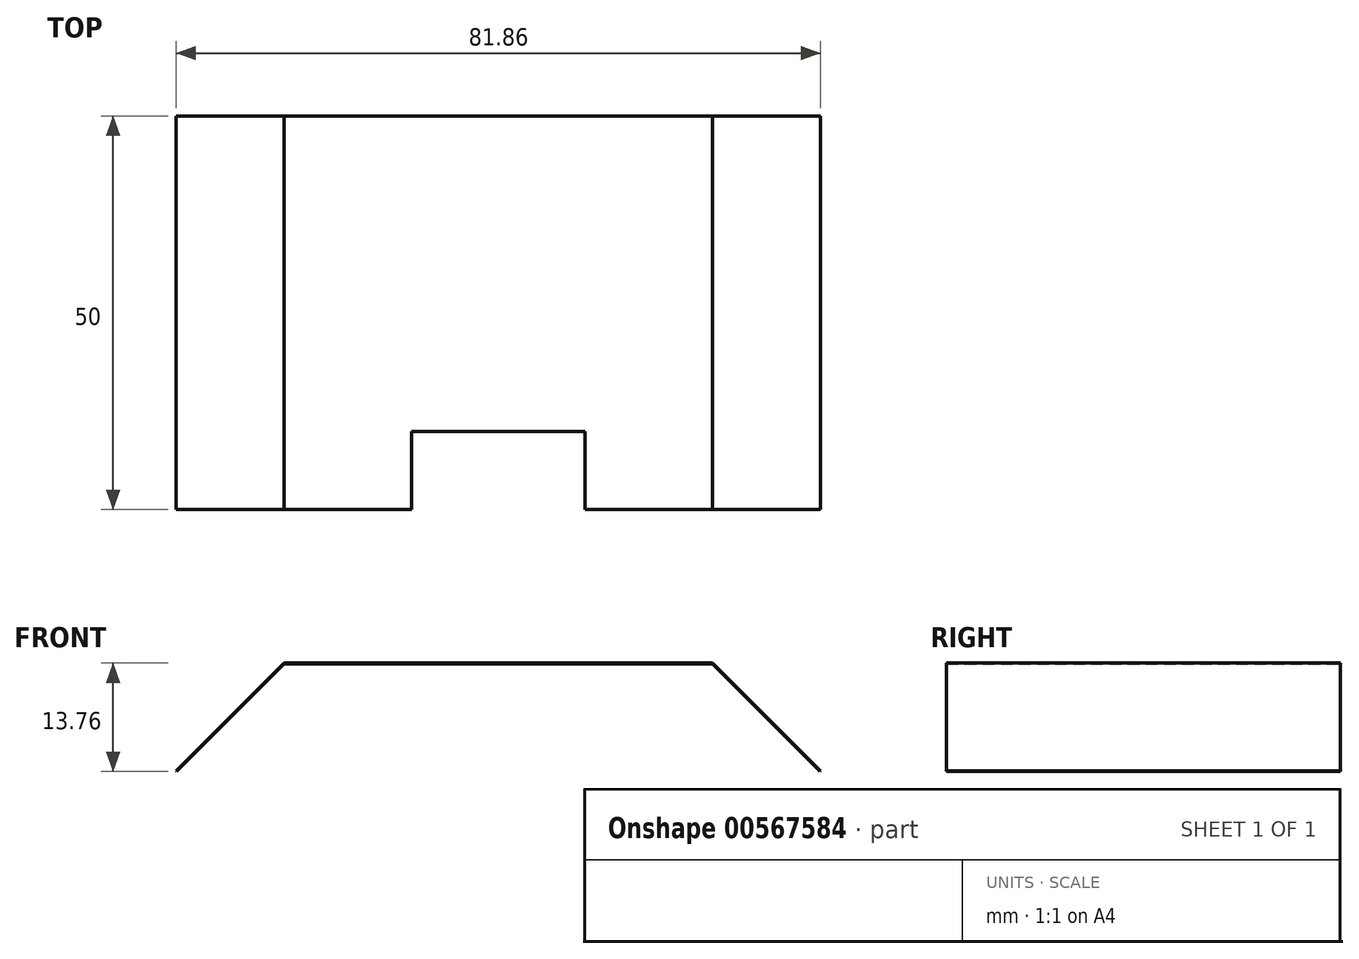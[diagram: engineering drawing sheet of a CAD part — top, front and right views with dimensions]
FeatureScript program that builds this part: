
annotation { "Feature Type Name" : "Feature", "Feature Type Description" : "" }
export const myFeature = defineFeature(function(context is Context, id is Id, definition is map)
    precondition{}
    {
        {
            var Q0;
            Q0=qCreatedBy(makeId("Front.planeOp"),FACE);
            var sketch = newSketch(context, id + "F0", { "sketchPlane" : qUnion([Q0])});
            skLineSegment(sketch, "E0", {"start": v(0, 0) * mm, "end": v(13.65, 13.65) * mm});
            skLineSegment(sketch, "E1", {"start": v(13.65, 13.65) * mm, "end": v(68.04, 13.65) * mm});
            skLineSegment(sketch, "E2", {"start": v(68.04, 13.65) * mm, "end": v(81.7, 0) * mm});
            skLineSegment(sketch, "E3.0", {"start": v(68.09, 13.76) * mm, "end": v(80.92, 0.92) * mm});
            skLineSegment(sketch, "E3.1", {"start": v(13.6, 13.76) * mm, "end": v(68.09, 13.76) * mm});
            skLineSegment(sketch, "E3.2", {"start": v(-0.08, 0.08) * mm, "end": v(13.6, 13.76) * mm});
            skLineSegment(sketch, "E4", {"start": v(-0.08, 0.08) * mm, "end": v(0, 0) * mm});
            skLineSegment(sketch, "E5", {"start": v(80.92, 0.92) * mm, "end": v(81.78, 0.06) * mm});
            skLineSegment(sketch, "E6", {"start": v(81.78, 0.06) * mm, "end": v(81.7, 0) * mm});
            skSolve(sketch);
        }
        {
            var Q0;
            Q0=makeQuery(id+"F0.imprint","IMPRINT",FACE,{"disambiguationData":[TD([[makeQuery(id+"F0.imprint","IMPRINT",EDGE,{"derivedFrom":sQuery(id+"F0.wireOp",EDGE,"E0")}),1.0]])]});
            extrude(context, id + "F1", {"entities" : qUnion([Q0]), "depth" : 50 * mm, "offsetDistance" : 25 * mm});
        }
        {
            var Q0;
            Q0=makeQuery(id+"F1.opExtrude","SWEPT_FACE",FACE,{"disambiguationData":[OSD([sQuery(id+"F0.wireOp",EDGE,"E3.1")])]});
            var sketch = newSketch(context, id + "F2", { "sketchPlane" : qUnion([Q0])});
            skLineSegment(sketch, "E7", {"start": v(40.85, -50) * mm, "end": v(40.85, 0) * mm, "construction": true});
            skLineSegment(sketch, "E8", {"start": v(29.85, -50) * mm, "end": v(29.85, -40.5) * mm});
            skLineSegment(sketch, "E9", {"start": v(29.85, -40.5) * mm, "end": v(51.85, -40.5) * mm});
            skLineSegment(sketch, "E10", {"start": v(51.85, -40.5) * mm, "end": v(51.85, -50) * mm});
            skSolve(sketch);
        }
        {
            var Q0;
            {var subQ0=sQuery(id+"F2.wireOp",EDGE,"E8");Q0=makeQuery(id+"F2.imprint","IMPRINT",FACE,{"disambiguationData":[TD([[makeQuery(id+"F2.imprint","IMPRINT",EDGE,{"derivedFrom":subQ0}),-1.0]])]});}
            extrude(context, id + "F3", {"entities" : qUnion([Q0]), "operationType" : NewBodyOperationType.REMOVE, "endBound" : BoundingType.THROUGH_ALL, "oppositeDirection" : true, "depth" : 25 * mm, "offsetDistance" : 25 * mm});
        }
        {
            var Q0;
            Q0=makeQuery(id+"F3.boolean.opBoolean","COPY",FACE,{"derivedFrom":makeQuery(id+"F3.opExtrude","SWEPT_FACE",FACE,{"disambiguationData":[OSD([sQuery(id+"F2.wireOp",EDGE,"E9")])]})});
            extrude(context, id + "F4", {"entities" : qUnion([Q0]), "operationType" : NewBodyOperationType.REMOVE, "oppositeDirection" : true, "depth" : 0.4 * mm, "offsetDistance" : 25 * mm});
        }
    });
